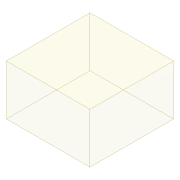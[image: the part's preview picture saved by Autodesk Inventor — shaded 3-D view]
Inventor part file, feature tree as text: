
AUTODESK INVENTOR PART (.ipt)
format: ipt  version: 2017 (Build 210142000, 142)  size: 72,704 bytes
history: native  units: mm
features: extrude x1, sketch x1
ambient origin geometry x8: Origin, YZ Plane, XZ Plane, XY Plane, X Axis, Y Axis, Z Axis, Center Point
bodies: Solid1 (feature_tree)
feature tree (2):
  extrude  "Extrusion1"  Depth=30.0mm
  sketch  "Sketch1"  dims[d0=30.0mm d1=30.0mm d2=18.0mm d3=0.0mm]
